# Revit family: Gira_201400
name_source: partatom
category: Elektroinstallationen
revit_build: Autodesk Revit 2017 (Build: 20160225_1515(x64)
units: mm (PartAtom-declared; Revit-internal decimal feet)

## family parameters
Basisbauteil = Fläche
Beim Laden mit Abzugskörper schneiden = Nein
Bemaßung runder Anschluss = Durchmesser verwenden
Beschriftungsausrichtung beibehalten = Nein
Gemeinsam genutzt = Nein
Raumberechnungspunkt = Nein
Teiletyp = Normal

## types (1)
- USB-Datenschnittst. REG KNX REG
    Andere Bussysteme = ohne
    Anzahl der Eingänge = 0
    Ausführung Text = USB
    Ausführung der Oberfläche = nicht zutreffend
    BIM = https://media.stage.bim.site X1 REG KNX.rfa
    BIMSITE_PRODUCT_ID = 04f23a842058d81640a22a3f83dca06389e7449b
    Beschreibung = KNX USB-Datenschnittstelle  REG Merkmale:  Ankopplung von PC an KNX Anlagen.  Adressierung, Programmierung und Diagnose von KNX Geräten.  Kompatibel zu KNX Data-Secure-Produkten.  Schneller Download der Applikationen (Long Frame Unterstützung ab ETS5).  Kompatibel zu ETS4, ETS5 (und höher).  Hinweise :  Kompatibel zum Gira HomeServer ab Version 4.9.  Montage auf DIN-Hutschiene.
    Breite in Teilungseinheiten = 2
    Bussystem Funkbus = Nein
    Bussystem KNX = Ja
    Bussystem KNX-Funk = Nein
    Bussystem LON = Nein
    Bussystem Powernet = Nein
    Datenblatt = https://media.stage.bim.site
    Datenblatt 1 = https://media.stage.bim.site
    Farbe = sonstige
    Funk bidirektional = Nein
    Funktion Schalten = Nein
    GTIN = 4010337072928
    HAN = 201400
    HeinzeBIM = https://www.heinze.de
    Hersteller = Gira
    Kosten = 0 $
    Max. Anzahl der Jalousieausgänge = 0
    Max. Schaltleistung [Voltampere] = 0
    Mit Beschriftungsfeld = Ja
    Mit Busankopplung = Ja
    Mit LED-Anzeige = Nein
    Montageart = REG
    Oberfläche Text = sonstige
    Produktseite = https://media.stage.bim.site
    Schutzart (IP) = IP20
    Transparent = Nein
    Typname = USB-Datenschnittst. REG KNX REG
    URL = https://www.gira.de
    Vor Ort-/Handbedienung = Nein
    Vorgabe-Ansicht = 1219 mm
    Werkstoff Text = Kunststoff
    Werkstoffgüte = Thermoplast

## geometry (parser evidence)
native form markers: Sweep x2
no freeform markers — native parametric forms only
